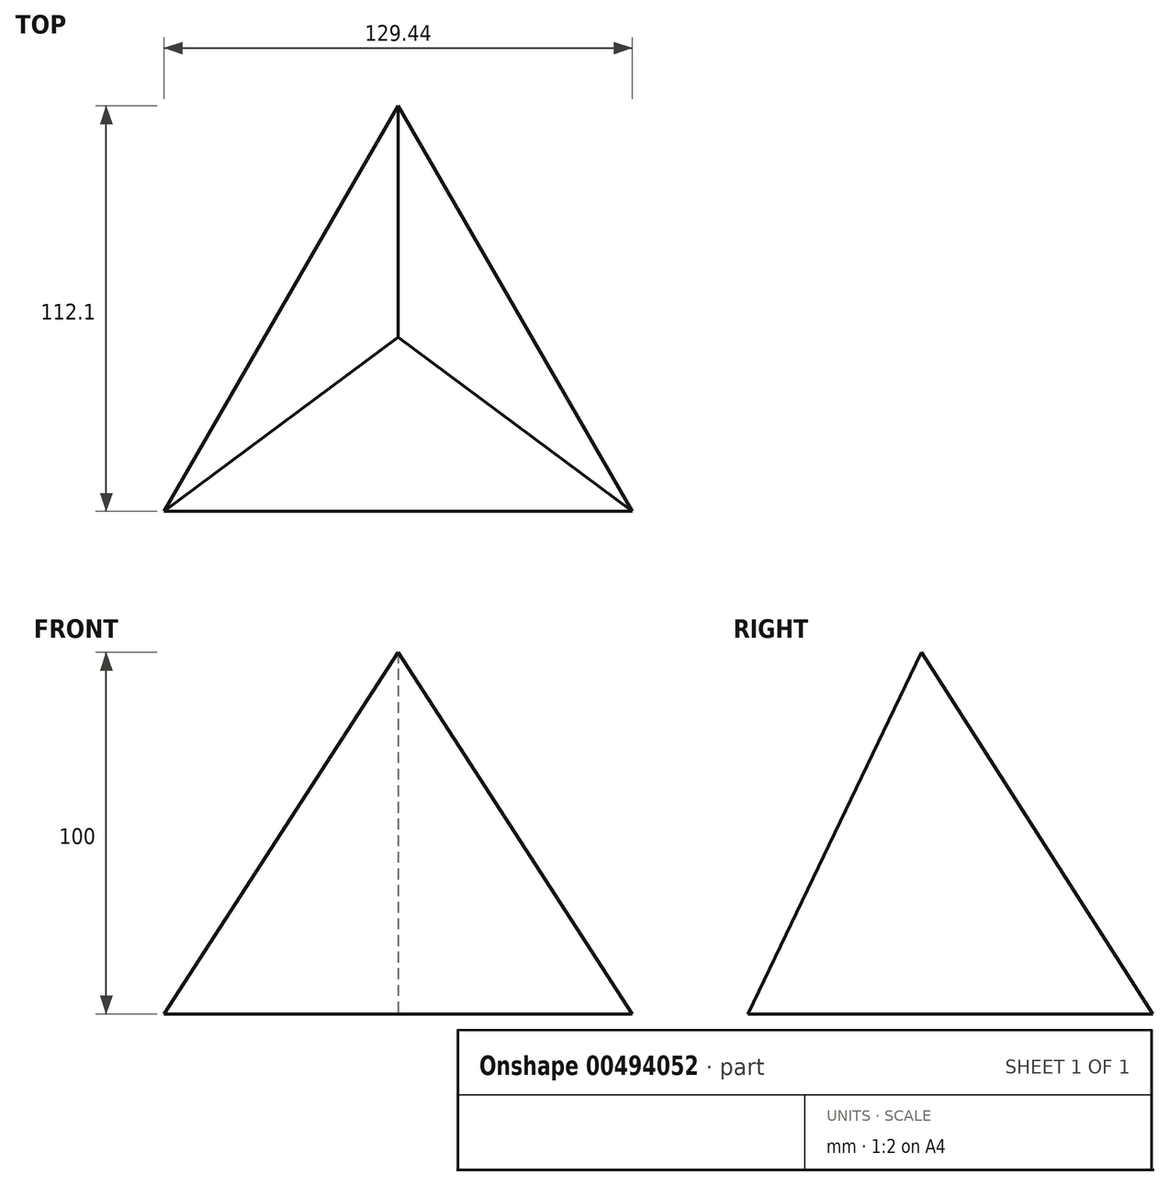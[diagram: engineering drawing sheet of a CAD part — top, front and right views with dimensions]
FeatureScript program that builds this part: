
annotation { "Feature Type Name" : "Feature", "Feature Type Description" : "" }
export const myFeature = defineFeature(function(context is Context, id is Id, definition is map)
    precondition{}
    {
        {
            var Q0;
            Q0=qCreatedBy(makeId("Top.planeOp"),FACE);
            var sketch = newSketch(context, id + "F0", { "sketchPlane" : qUnion([Q0])});
            skCircle(sketch, "E0.cCircle", {"center": v(0, 0) * mm, "radius": 74.73 * mm, "construction": true});
            skLineSegment(sketch, "E0.0", {"start": v(0, 74.73) * mm, "end": v(64.72, -37.37) * mm});
            skLineSegment(sketch, "E0.1", {"start": v(64.72, -37.37) * mm, "end": v(-64.72, -37.37) * mm});
            skLineSegment(sketch, "E0.2", {"start": v(-64.72, -37.37) * mm, "end": v(0, 74.73) * mm});
            skSolve(sketch);
        }
        {
            var Q0;
            Q0=qCreatedBy(makeId("Top.planeOp"),FACE);
            cPlane(context, id + "F1", {"entities" : qUnion([Q0]), "cplaneType" : CPlaneType.OFFSET, "offset" : 100 * mm, "width" : 150 * mm, "height" : 150 * mm});
        }
        {
            var Q0;
            Q0=qCreatedBy(id+"F1.planeOp",FACE);
            var sketch = newSketch(context, id + "F2", { "sketchPlane" : qUnion([Q0])});
            skPoint(sketch, "E1", {"position": v(0, 10.76) * mm});
            skSolve(sketch);
        }
        {
            var Q0;
            Q0=sQuery(id+"F2.wireOp",VERTEX,"E1");
            var Q1;
            Q1=makeQuery(id+"F0.imprint","IMPRINT",FACE,{"disambiguationData":[TD([[makeQuery(id+"F0.imprint","IMPRINT",EDGE,{"derivedFrom":sQuery(id+"F0.wireOp",EDGE,"E0.0")}),-1.0]])]});
            loft(context, id + "F3", {"sheetProfilesArray" : [{ "sheetProfileEntities" : qUnion([Q0]) }, { "sheetProfileEntities" : qUnion([Q1]) }]});
        }
    });
